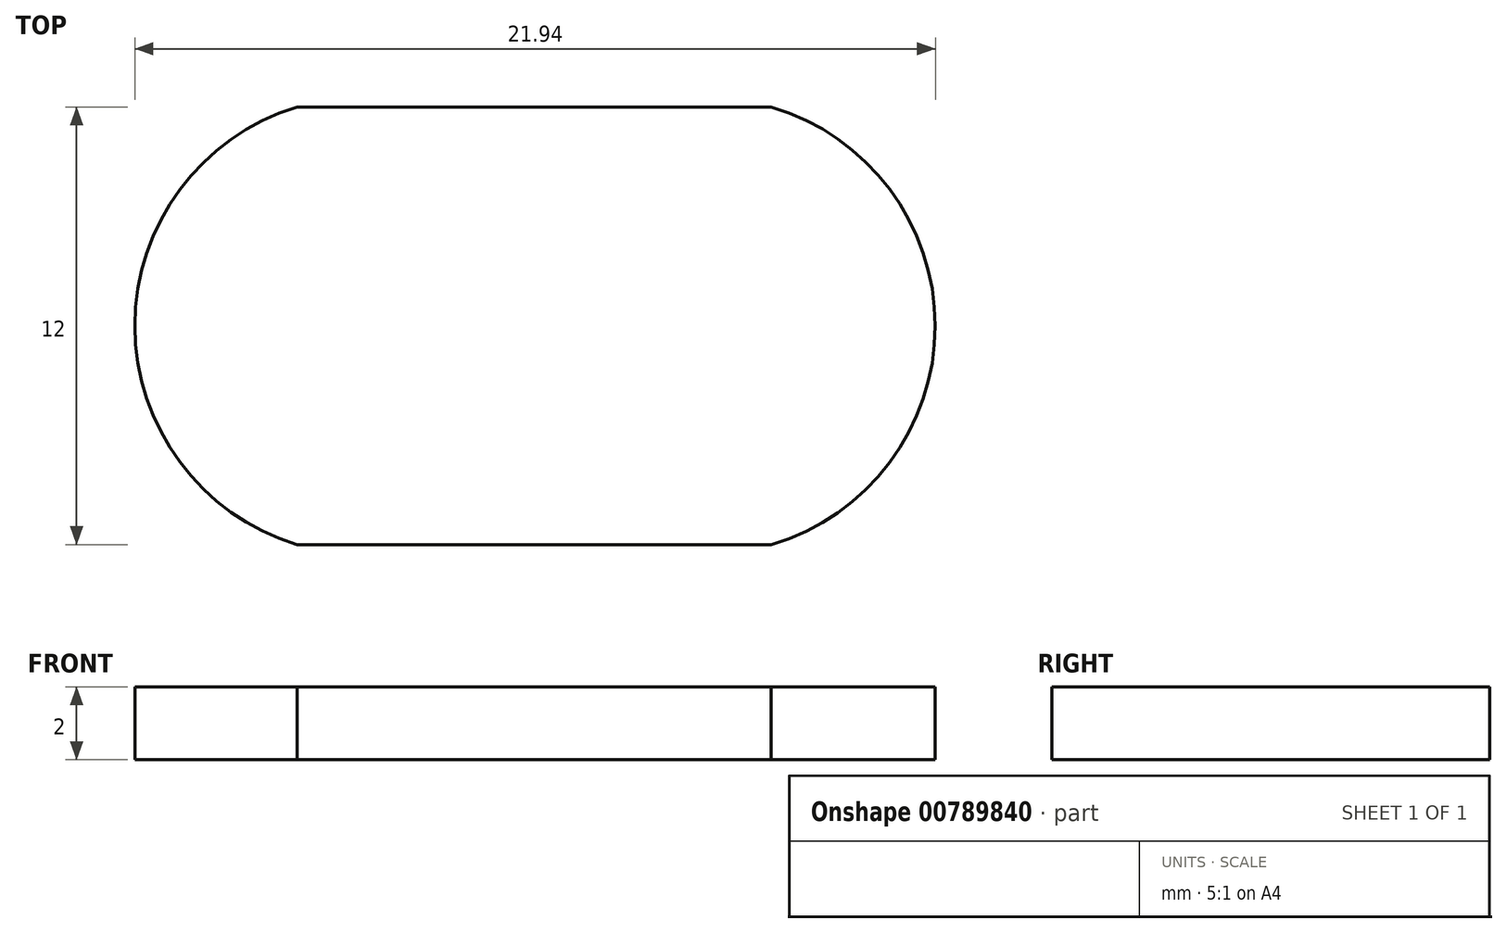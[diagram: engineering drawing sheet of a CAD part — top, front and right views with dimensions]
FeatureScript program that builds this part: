
annotation { "Feature Type Name" : "Feature", "Feature Type Description" : "" }
export const myFeature = defineFeature(function(context is Context, id is Id, definition is map)
    precondition{}
    {
        {
            var Q0;
            Q0=qCreatedBy(makeId("Top.planeOp"),FACE);
            var sketch = newSketch(context, id + "F0", { "sketchPlane" : qUnion([Q0])});
            skLineSegment(sketch, "E0.bottom", {"start": v(6.5, -6) * mm, "end": v(-6.5, -6) * mm});
            skLineSegment(sketch, "E0.top", {"start": v(6.5, 6) * mm, "end": v(-6.5, 6) * mm});
            skPoint(sketch, "E0.middle", {"position": v(0, 0) * mm});
            skLineSegment(sketch, "E1", {"start": v(-11, 7.8) * mm, "end": v(-11, -7.92) * mm, "construction": true});
            skLineSegment(sketch, "E2", {"start": v(11, 7.83) * mm, "end": v(11, -8.37) * mm, "construction": true});
            skArc(sketch, "E3", {"start": v(-6.5, 6) * mm, "mid": v(-10.94, 0) * mm, "end": v(-6.5, -6) * mm});
            skArc(sketch, "E4", {"start": v(6.5, -6) * mm, "mid": v(11, 0) * mm, "end": v(6.5, 6) * mm});
            skSolve(sketch);
        }
        {
            var Q0;
            Q0=makeQuery(id+"F0.imprint","IMPRINT",FACE,{"disambiguationData":[TD([[makeQuery(id+"F0.imprint","IMPRINT",EDGE,{"derivedFrom":sQuery(id+"F0.wireOp",EDGE,"E0.bottom")}),-1.0]])]});
            extrude(context, id + "F1", {"entities" : qUnion([Q0]), "depth" : 2 * mm, "offsetDistance" : 25 * mm});
        }
    });
